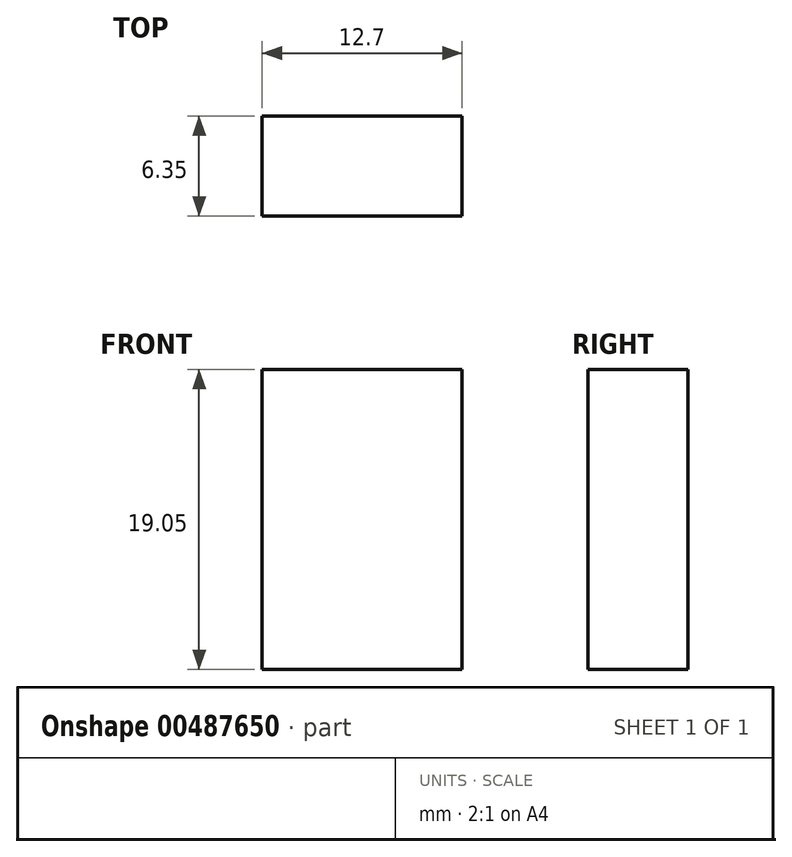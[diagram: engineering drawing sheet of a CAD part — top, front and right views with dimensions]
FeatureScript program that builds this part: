
annotation { "Feature Type Name" : "Feature", "Feature Type Description" : "" }
export const myFeature = defineFeature(function(context is Context, id is Id, definition is map)
    precondition{}
    {
        {
            var Q0;
            Q0=qCreatedBy(makeId("Front.planeOp"),FACE);
            var sketch = newSketch(context, id + "F0", { "sketchPlane" : qUnion([Q0])});
            skLineSegment(sketch, "E0.bottom", {"start": v(0, 0) * mm, "end": v(12.7, 0) * mm});
            skLineSegment(sketch, "E0.top", {"start": v(0, 19.05) * mm, "end": v(12.7, 19.05) * mm});
            skLineSegment(sketch, "E0.left", {"start": v(0, 0) * mm, "end": v(0, 19.05) * mm});
            skLineSegment(sketch, "E0.right", {"start": v(12.7, 0) * mm, "end": v(12.7, 19.05) * mm});
            skSolve(sketch);
        }
        {
            var Q0;
            Q0 = qSketchRegion(id + "F0", true);
            extrude(context, id + "F1", {"entities" : qUnion([Q0]), "depth" : 6.35 * mm});
        }
    });
